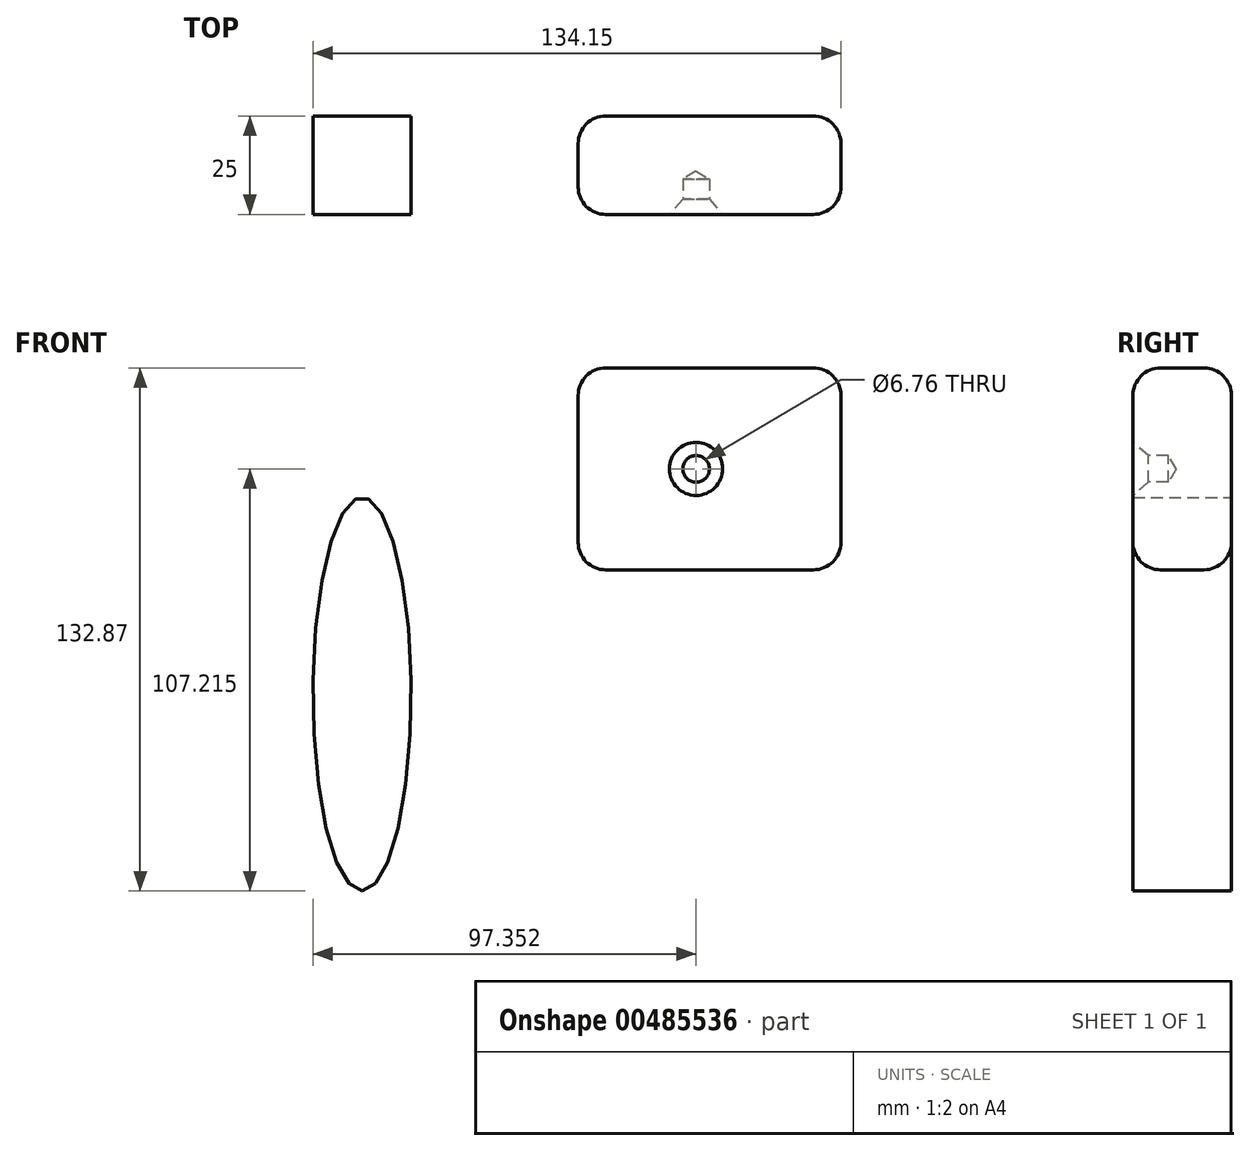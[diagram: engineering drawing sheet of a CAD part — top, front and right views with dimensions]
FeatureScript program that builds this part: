
annotation { "Feature Type Name" : "Feature", "Feature Type Description" : "" }
export const myFeature = defineFeature(function(context is Context, id is Id, definition is map)
    precondition{}
    {
        {
            var Q0;
            Q0=qCreatedBy(makeId("Front.planeOp"),FACE);
            var sketch = newSketch(context, id + "F0", { "sketchPlane" : qUnion([Q0])});
            skLineSegment(sketch, "E0.bottom", {"start": v(-92.8, 13.27) * mm, "end": v(-26.04, 13.27) * mm});
            skLineSegment(sketch, "E0.top", {"start": v(-92.8, 64.58) * mm, "end": v(-26.04, 64.58) * mm});
            skLineSegment(sketch, "E0.left", {"start": v(-92.8, 13.27) * mm, "end": v(-92.8, 64.58) * mm});
            skLineSegment(sketch, "E0.right", {"start": v(-26.04, 13.27) * mm, "end": v(-26.04, 64.58) * mm});
            skPoint(sketch, "E0.middle", {"position": v(-59.41, 38.92) * mm});
            skSolve(sketch);
        }
        {
            var Q0;
            Q0=makeQuery(id+"F0.imprint","IMPRINT",FACE,{"disambiguationData":[TD([[makeQuery(id+"F0.imprint","IMPRINT",EDGE,{"derivedFrom":sQuery(id+"F0.wireOp",EDGE,"E0.bottom")}),1.0]])]});
            extrude(context, id + "F1", {"entities" : qUnion([Q0]), "depth" : 25 * mm});
        }
        {
            var Q0;
            Q0=makeQuery(id+"F1.opExtrude","SWEPT_FACE",FACE,{"disambiguationData":[OSD([sQuery(id+"F0.wireOp",EDGE,"E0.bottom")])]});
            var Q1;
            Q1=makeQuery(id+"F1.opExtrude","CAP_FACE",FACE,{"disambiguationData":[OSD([sQuery(id+"F0.wireOp",EDGE,"E0.bottom"),sQuery(id+"F0.wireOp",EDGE,"E0.top"),sQuery(id+"F0.wireOp",EDGE,"E0.left"),sQuery(id+"F0.wireOp",EDGE,"E0.right")])],"isStart":true});
            var Q2;
            Q2=makeQuery(id+"F1.opExtrude","SWEPT_EDGE",EDGE,{"disambiguationData":[OSD([sQuery(id+"F0.wireOp",EDGE,"E0.top"),sQuery(id+"F0.wireOp",EDGE,"E0.left")])]});
            var Q3;
            Q3=makeQuery(id+"F1.opExtrude","CAP_FACE",FACE,{"disambiguationData":[OSD([sQuery(id+"F0.wireOp",EDGE,"E0.bottom"),sQuery(id+"F0.wireOp",EDGE,"E0.top"),sQuery(id+"F0.wireOp",EDGE,"E0.left"),sQuery(id+"F0.wireOp",EDGE,"E0.right")])],"isStart":false});
            var Q4;
            Q4=makeQuery(id+"F1.opExtrude","SWEPT_EDGE",EDGE,{"disambiguationData":[OSD([sQuery(id+"F0.wireOp",EDGE,"E0.top"),sQuery(id+"F0.wireOp",EDGE,"E0.right")])]});
            var Q5;
            Q5=makeQuery(id+"F1.opExtrude","SWEPT_FACE",FACE,{"disambiguationData":[OSD([sQuery(id+"F0.wireOp",EDGE,"E0.top")])]});
            var Q6;
            Q6=makeQuery(id+"F1.opExtrude","SWEPT_FACE",FACE,{"disambiguationData":[OSD([sQuery(id+"F0.wireOp",EDGE,"E0.left")])]});
            var Q7;
            Q7=makeQuery(id+"F1.opExtrude","CAP_EDGE",EDGE,{"disambiguationData":[OSD([sQuery(id+"F0.wireOp",EDGE,"E0.bottom")])],"isStart":false});
            var Q8;
            Q8=makeQuery(id+"F1.opExtrude","SWEPT_FACE",FACE,{"disambiguationData":[OSD([sQuery(id+"F0.wireOp",EDGE,"E0.right")])]});
            var Q9;
            Q9=makeQuery(id+"F1.opExtrude","CAP_EDGE",EDGE,{"disambiguationData":[OSD([sQuery(id+"F0.wireOp",EDGE,"E0.top")])],"isStart":true});
            var Q10;
            Q10=makeQuery(id+"F1.opExtrude","CAP_EDGE",EDGE,{"disambiguationData":[OSD([sQuery(id+"F0.wireOp",EDGE,"E0.top")])],"isStart":false});
            var Q11;
            Q11=makeQuery(id+"F1.opExtrude","SWEPT_EDGE",EDGE,{"disambiguationData":[OSD([sQuery(id+"F0.wireOp",EDGE,"E0.bottom"),sQuery(id+"F0.wireOp",EDGE,"E0.left")])]});
            var Q12;
            Q12=makeQuery(id+"F1.opExtrude","SWEPT_EDGE",EDGE,{"disambiguationData":[OSD([sQuery(id+"F0.wireOp",EDGE,"E0.bottom"),sQuery(id+"F0.wireOp",EDGE,"E0.right")])]});
            var Q13;
            Q13=makeQuery(id+"F1.opExtrude","CAP_EDGE",EDGE,{"disambiguationData":[OSD([sQuery(id+"F0.wireOp",EDGE,"E0.bottom")])],"isStart":true});
            var Q14;
            Q14=makeQuery(id+"F1.opExtrude","CAP_EDGE",EDGE,{"disambiguationData":[OSD([sQuery(id+"F0.wireOp",EDGE,"E0.left")])],"isStart":true});
            var Q15;
            Q15=makeQuery(id+"F1.opExtrude","CAP_EDGE",EDGE,{"disambiguationData":[OSD([sQuery(id+"F0.wireOp",EDGE,"E0.left")])],"isStart":false});
            var Q16;
            Q16=makeQuery(id+"F1.opExtrude","CAP_EDGE",EDGE,{"disambiguationData":[OSD([sQuery(id+"F0.wireOp",EDGE,"E0.right")])],"isStart":true});
            var Q17;
            Q17=makeQuery(id+"F1.opExtrude","CAP_EDGE",EDGE,{"disambiguationData":[OSD([sQuery(id+"F0.wireOp",EDGE,"E0.right")])],"isStart":false});
            fillet(context, id + "F2", {"entities" : qUnion([Q0, Q1, Q2, Q3, Q4, Q5, Q6, Q7, Q8, Q9, Q10, Q11, Q12, Q13, Q14, Q15, Q16, Q17]), "radius" : 7 * mm, "tangentPropagation" : true, "allowEdgeOverflow" : false});
        }
        {
            var Q0;
            Q0=qCreatedBy(makeId("Front.planeOp"),FACE);
            var sketch = newSketch(context, id + "F3", { "sketchPlane" : qUnion([Q0])});
            skEllipse(sketch, "E1", {"center": v(-147.69, -18.3) * mm, "majorRadius": 50 * mm, "minorRadius": 12.5 * mm, "majorAxis": v(0, -1)});
            skSolve(sketch);
        }
        {
            var Q0;
            Q0=makeQuery(id+"F3.imprint","IMPRINT",FACE,{"disambiguationData":[TD([[makeQuery(id+"F3.imprint","IMPRINT",EDGE,{"derivedFrom":sQuery(id+"F3.wireOp",EDGE,"E1")}),1.0]])]});
            extrude(context, id + "F4", {"entities" : qUnion([Q0]), "depth" : 25 * mm});
        }
        {
            var Q0;
            Q0=makeQuery(id+"F1.opExtrude","CAP_FACE",FACE,{"disambiguationData":[OSD([sQuery(id+"F0.wireOp",EDGE,"E0.bottom"),sQuery(id+"F0.wireOp",EDGE,"E0.top"),sQuery(id+"F0.wireOp",EDGE,"E0.left"),sQuery(id+"F0.wireOp",EDGE,"E0.right")])],"isStart":false});
            var sketch = newSketch(context, id + "F5", { "sketchPlane" : qUnion([Q0])});
            skPoint(sketch, "E2", {"position": v(-62.84, 38.92) * mm});
            skPoint(sketch, "E2.positionSnap0", {"position": v(-85.8, 38.92) * mm});
            skSolve(sketch);
        }
        {
            var Q0;
            Q0=sQuery(id+"F5.wireOp",VERTEX,"E2");
            var Q1;
            Q1=makeQuery(id+"F1.opExtrude","SWEPT_BODY",BODY,{"disambiguationData":[OSD([sQuery(id+"F0.wireOp",EDGE,"E0.bottom"),sQuery(id+"F0.wireOp",EDGE,"E0.top"),sQuery(id+"F0.wireOp",EDGE,"E0.left"),sQuery(id+"F0.wireOp",EDGE,"E0.right")])]});
            hole(context, id + "F6", {"style" : HoleStyle.C_SINK, "endStyle" : HoleEndStyle.BLIND, "standardTappedOrClearance" : lookupTablePath({ "standard" : "ANSI", "fit" : "Normal (ASME)", "size" : "1/4", "type" : "Clearance" }), "standardBlindInLast" : lookupTablePath({ "fit" : "Free", "standard" : "ANSI", "size" : "1/4", "type" : "Clearance" }), "holeDiameter" : 6.76 * mm, "cSinkDiameter" : 13.5 * mm, "cSinkAngle" : 82 * degree, "holeDepth" : 9 * mm, "isTappedThrough" : true, "tappedDepth" : 12 * mm, "tapClearance" : 3, "locations" : qUnion([Q0]), "scope" : qUnion([Q1])});
        }
    });
